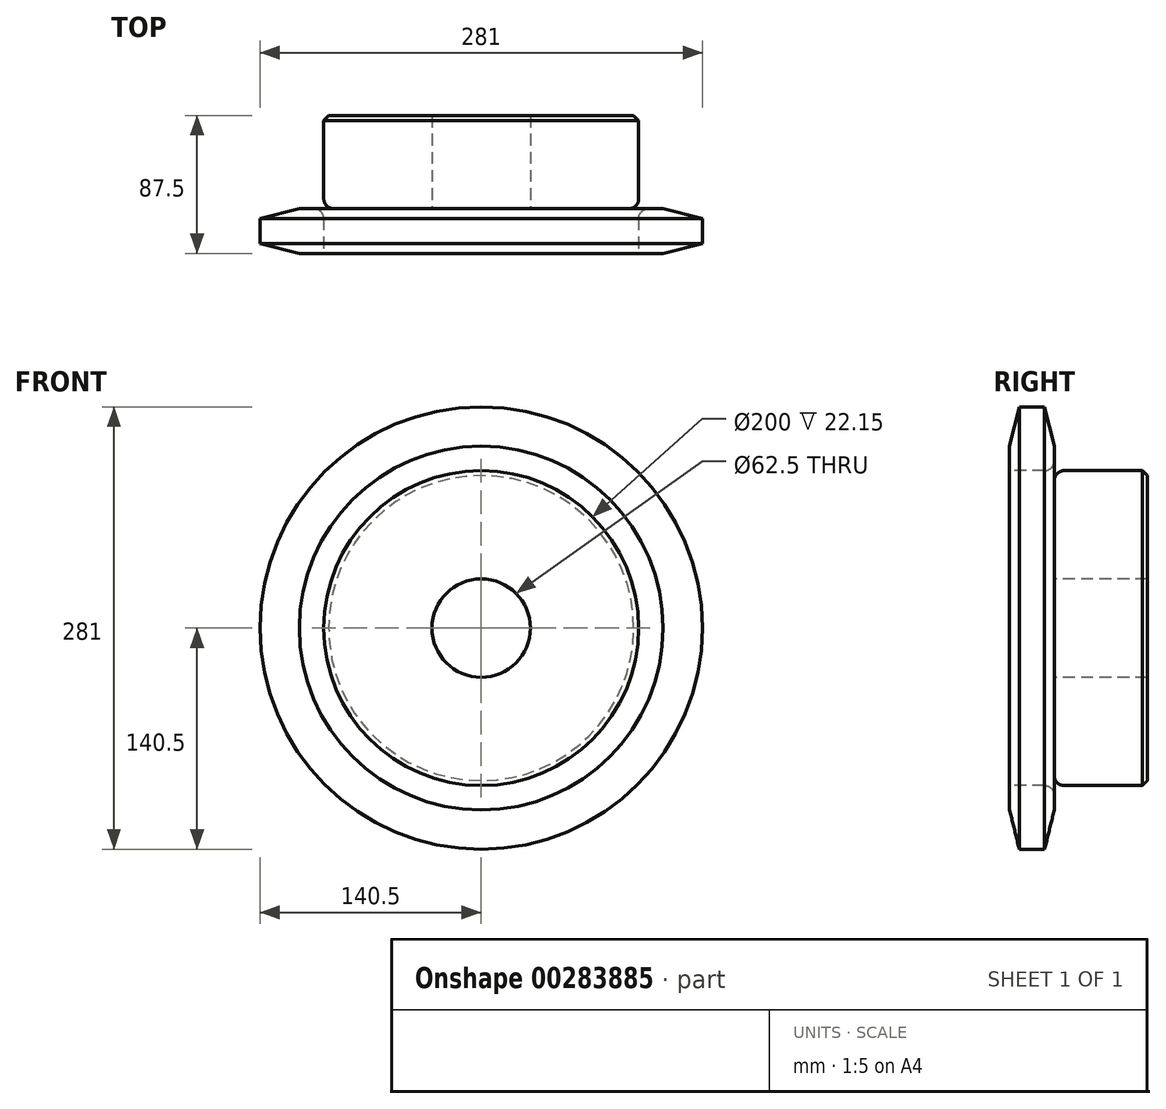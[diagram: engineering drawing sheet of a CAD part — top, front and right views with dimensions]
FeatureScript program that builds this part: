
annotation { "Feature Type Name" : "Feature", "Feature Type Description" : "" }
export const myFeature = defineFeature(function(context is Context, id is Id, definition is map)
    precondition{}
    {
        {
            var Q0;
            Q0=qCreatedBy(makeId("Right.planeOp"),FACE);
            var sketch = newSketch(context, id + "F0", { "sketchPlane" : qUnion([Q0])});
            skLineSegment(sketch, "E0", {"start": v(0, 0) * mm, "end": v(87.5, 0) * mm, "construction": true});
            skLineSegment(sketch, "E1.bottom", {"start": v(0, 31.25) * mm, "end": v(28.4, 31.25) * mm});
            skLineSegment(sketch, "E1.top", {"start": v(0, 140.5) * mm, "end": v(28.4, 140.5) * mm});
            skLineSegment(sketch, "E1.left", {"start": v(0, 31.25) * mm, "end": v(0, 140.5) * mm});
            skLineSegment(sketch, "E1.right", {"start": v(28.4, 31.25) * mm, "end": v(28.4, 140.5) * mm});
            skLineSegment(sketch, "E2.bottom", {"start": v(0, 31.25) * mm, "end": v(87.5, 31.25) * mm});
            skLineSegment(sketch, "E2.top", {"start": v(0, 100) * mm, "end": v(87.5, 100) * mm});
            skLineSegment(sketch, "E2.left", {"start": v(0, 31.25) * mm, "end": v(0, 100) * mm});
            skLineSegment(sketch, "E2.right", {"start": v(87.5, 31.25) * mm, "end": v(87.5, 100) * mm});
            skLineSegment(sketch, "E3.MirrorCS", {"start": v(0, -31.25) * mm, "end": v(28.4, -31.25) * mm});
            skLineSegment(sketch, "E4.MirrorCS", {"start": v(87.5, -31.25) * mm, "end": v(87.5, -100) * mm});
            skLineSegment(sketch, "E5.MirrorCS", {"start": v(0, -31.25) * mm, "end": v(0, -100) * mm});
            skLineSegment(sketch, "E6.MirrorCS", {"start": v(0, -100) * mm, "end": v(87.5, -100) * mm});
            skLineSegment(sketch, "E7.MirrorCS", {"start": v(0, -31.25) * mm, "end": v(87.5, -31.25) * mm});
            skLineSegment(sketch, "E8.MirrorCS", {"start": v(28.4, -31.25) * mm, "end": v(28.4, -140.5) * mm});
            skLineSegment(sketch, "E9.MirrorCS", {"start": v(0, -31.25) * mm, "end": v(0, -140.5) * mm});
            skLineSegment(sketch, "E10.MirrorCS", {"start": v(0, -140.5) * mm, "end": v(28.4, -140.5) * mm});
            skSolve(sketch);
        }
        {
            var Q0;
            {var subQ0=sQuery(id+"F0.wireOp",EDGE,"E1.top");Q0=makeQuery(id+"F0.imprint","IMPRINT",FACE,{"disambiguationData":[TD([[makeQuery(id+"F0.imprint","IMPRINT",EDGE,{"derivedFrom":subQ0}),-1.0]])]});}
            var Q1;
            {var subQ5=sQuery(id+"F0.wireOp",EDGE,"E2.left");Q1=makeQuery(id+"F0.imprint","IMPRINT",FACE,{"disambiguationData":[TD([[makeQuery(id+"F0.imprint","IMPRINT",EDGE,{"derivedFrom":subQ5}),-1.0]])]});}
            var Q2;
            {var subQ5=sQuery(id+"F0.wireOp",EDGE,"E2.right");Q2=makeQuery(id+"F0.imprint","IMPRINT",FACE,{"disambiguationData":[TD([[makeQuery(id+"F0.imprint","IMPRINT",EDGE,{"derivedFrom":subQ5}),1.0]])]});}
            var Q3;
            Q3=sQuery(id+"F0.wireOp",EDGE,"E0");
            revolve(context, id + "F1", {"entities" : qUnion([Q0, Q1, Q2]), "axis" : qUnion([Q3]), "revolveType" : RevolveType.FULL});
        }
        {
            var Q0;
            Q0=makeQuery(id+"F1.opRevolve","SWEPT_EDGE",EDGE,{"disambiguationData":[OSD([sQuery(id+"F0.wireOp",EDGE,"E1.right"),sQuery(id+"F0.wireOp",EDGE,"E2.top")])]});
            fillet(context, id + "F2", {"entities" : qUnion([Q0]), "radius" : (100 / 16) * mm, "tangentPropagation" : true, "allowEdgeOverflow" : false});
        }
        {
            var Q0;
            Q0=makeQuery(id+"F1.opRevolve","SWEPT_EDGE",EDGE,{"disambiguationData":[OSD([sQuery(id+"F0.wireOp",EDGE,"E2.top"),sQuery(id+"F0.wireOp",EDGE,"E2.right")])]});
            chamfer(context, id + "F3", {"entities" : qUnion([Q0]), "width" : (100 / 32) * mm, "tangentPropagation" : true});
        }
        {
            var Q0;
            Q0=makeQuery(id+"F1.opRevolve","SWEPT_EDGE",EDGE,{"disambiguationData":[OSD([sQuery(id+"F0.wireOp",EDGE,"E1.top"),sQuery(id+"F0.wireOp",EDGE,"E1.left")])]});
            var Q1;
            Q1=makeQuery(id+"F1.opRevolve","SWEPT_EDGE",EDGE,{"disambiguationData":[OSD([sQuery(id+"F0.wireOp",EDGE,"E1.top"),sQuery(id+"F0.wireOp",EDGE,"E1.right")])]});
            chamfer(context, id + "F4", {"entities" : qUnion([Q0, Q1]), "chamferType" : ChamferType.TWO_OFFSETS, "width1" : 25 * mm, "oppositeDirection" : false, "width2" : 6.2 * mm, "tangentPropagation" : true});
        }
    });
